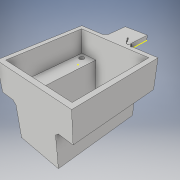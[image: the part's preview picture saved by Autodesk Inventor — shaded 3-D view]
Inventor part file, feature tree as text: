
AUTODESK INVENTOR PART (.ipt)
format: ipt  version: 2019 (Build 230136000, 136)  size: 241,664 bytes
history: native  units: mm
features: sketch x8, projected_geometry x8, extrude x7, chamfer x3
ambient origin geometry x8: Origin, YZ Plane, XZ Plane, XY Plane, X Axis, Y Axis, Z Axis, Center Point
bodies: Solid1 (feature_tree)
feature tree (26):
  extrude  "Extrusion1"  Depth=16.1mm
  extrude  "Extrusion2"  Depth=29.0mm
  extrude  "Extrusion3"  Depth=54.0mm
  extrude  "Extrusion4"  Depth=14.25mm
  extrude  "Extrusion5"  Depth=3.0mm TaperAngle=0.0deg
  chamfer  "Chamfer1"  Distance=25.0mm
  chamfer  "Chamfer2"  Distance=3.0mm
  extrude  "Extrusion6"  Depth=45.0mm
  extrude  "Extrusion7"  Depth=48.0mm
  chamfer  "Chamfer3"  Distance=15.0mm
  sketch  "Sketch8"  dims[d15=51.0mm d16=3.0mm d17=0.0mm d18=45.0mm d19=48.0mm d20=15.0mm d21=0.0mm d22=3.5mm d23=4.0mm d24=4.0mm d25=4.0mm d26=20.0mm d28=40.0mm d29=20.0mm d31=37.0mm d34=10.0mm d35=0.0mm d36=2.0mm d37=2.0mm d38=45.0deg d39=2.0mm d40=2.0mm d41=45.0deg d42=6.0mm d43=20.0mm d45=40.0mm d46=20.0mm d48=37.0mm d51=10.0mm d52=0.0mm d53=4.0mm d54=15.0mm d55=3.0mm d56=18.0mm d57=18.0mm d58=16.0mm d59=0.0mm d60=2.0mm d61=2.0mm d62=45.0deg d63=6.0mm]
  sketch  "Sketch1"  dims[d0=16.1mm d1=16.1mm]
  sketch  "Sketch2"  dims[d2=25.5mm d3=29.0mm]
  sketch  "Sketch3"  dims[d4=54.0mm d5=14.5mm]
  sketch  "Sketch4"  dims[d6=14.5mm d7=14.25mm]
  sketch  "Sketch5"  dims[d8=14.25mm d9=3.0mm d10=0.0mm]
  projected_geometry  "Projected Loop1"
  projected_geometry  "Projected Loop2"
  projected_geometry  "Projected Loop3"
  projected_geometry  "Projected Loop4"
  sketch  "Sketch6"  dims[d11=23.0mm]
  projected_geometry  "Projected Loop5"
  projected_geometry  "Projected Loop6"
  sketch  "Sketch7"  dims[d12=48.0mm d13=25.0mm d14=0.0mm]
  projected_geometry  "Projected Loop7"
  projected_geometry  "Projected Loop8"
